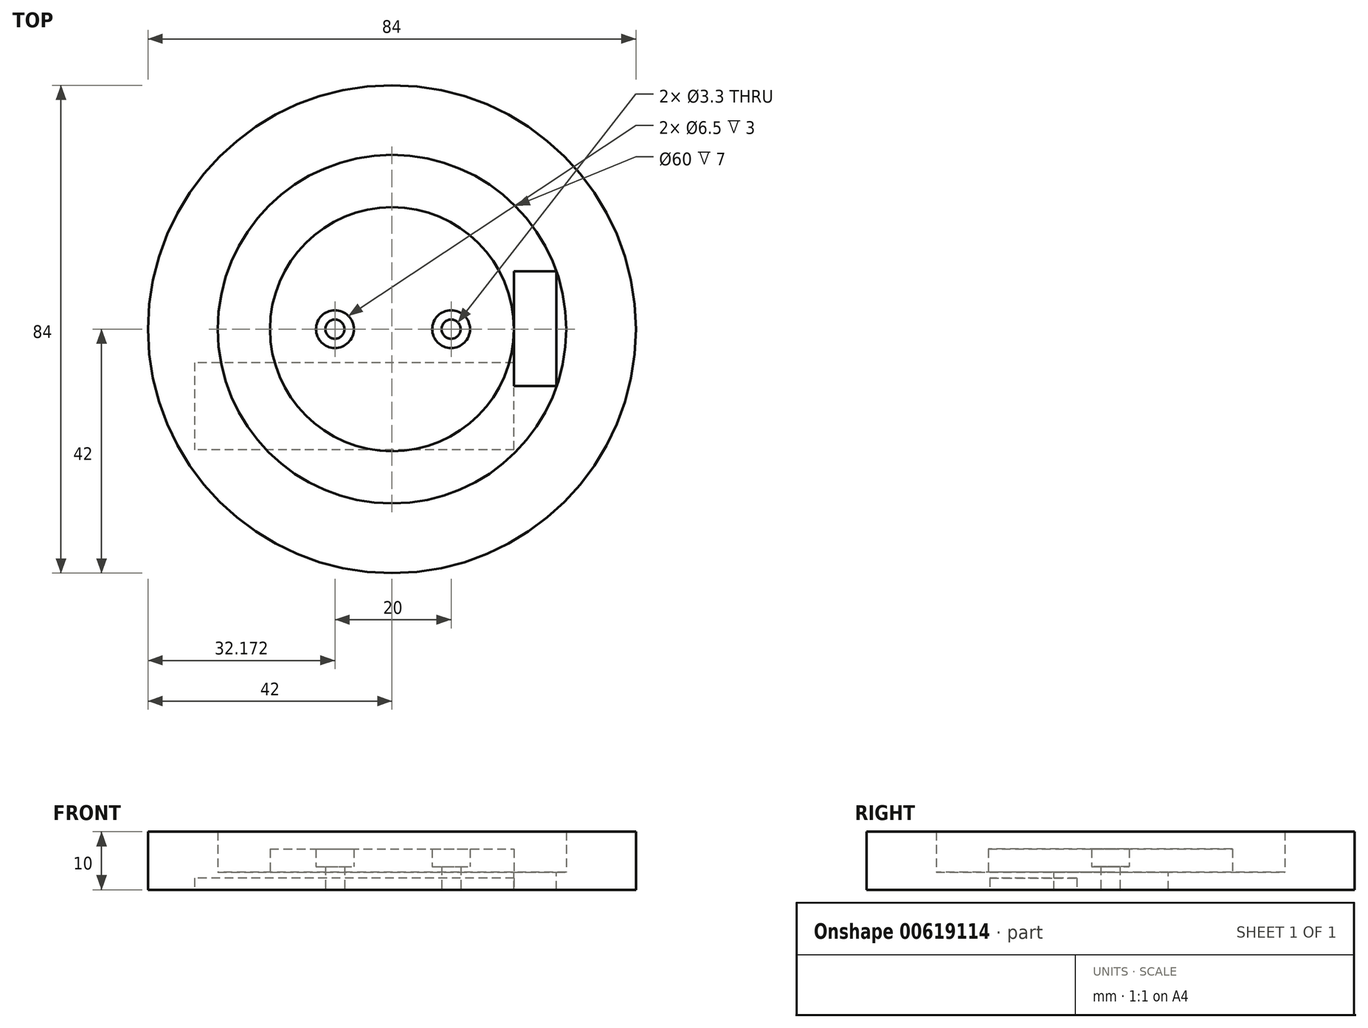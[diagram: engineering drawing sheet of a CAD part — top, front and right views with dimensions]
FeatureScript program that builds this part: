
annotation { "Feature Type Name" : "Feature", "Feature Type Description" : "" }
export const myFeature = defineFeature(function(context is Context, id is Id, definition is map)
    precondition{}
    {
        {
            var Q0;
            Q0=qCreatedBy(makeId("Front.planeOp"),FACE);
            var sketch = newSketch(context, id + "F0", { "sketchPlane" : qUnion([Q0])});
            skLineSegment(sketch, "E0", {"start": v(0, 0) * mm, "end": v(0, 7) * mm});
            skLineSegment(sketch, "E1", {"start": v(0, 7) * mm, "end": v(-21, 7) * mm});
            skLineSegment(sketch, "E2", {"start": v(-21, 7) * mm, "end": v(-21, 3) * mm});
            skLineSegment(sketch, "E3", {"start": v(-21, 3) * mm, "end": v(-30, 3) * mm});
            skLineSegment(sketch, "E4", {"start": v(-30, 3) * mm, "end": v(-30, 10) * mm});
            skLineSegment(sketch, "E5", {"start": v(-30, 10) * mm, "end": v(-42, 10) * mm});
            skLineSegment(sketch, "E6", {"start": v(-42, 10) * mm, "end": v(-42, 0) * mm});
            skLineSegment(sketch, "E7", {"start": v(-42, 0) * mm, "end": v(0, 0) * mm});
            skSolve(sketch);
        }
        {
            var Q0;
            Q0 = qSketchRegion(id + "F0", true);
            var Q1;
            Q1=sQuery(id+"F0.wireOp",EDGE,"E0");
            revolve(context, id + "F1", {"entities" : qUnion([Q0]), "axis" : qUnion([Q1]), "revolveType" : RevolveType.FULL});
        }
        {
            var Q0;
            Q0=makeQuery(id+"F1.opRevolve","SWEPT_FACE",FACE,{"disambiguationData":[OSD([sQuery(id+"F0.wireOp",EDGE,"E3")])]});
            var sketch = newSketch(context, id + "F2", { "sketchPlane" : qUnion([Q0])});
            skLineSegment(sketch, "E8.bottom", {"start": v(21, 0) * mm, "end": v(28.3, 0) * mm});
            skLineSegment(sketch, "E8.top", {"start": v(21, 9.97) * mm, "end": v(28.3, 9.97) * mm});
            skLineSegment(sketch, "E8.left", {"start": v(21, 0) * mm, "end": v(21, 9.97) * mm});
            skLineSegment(sketch, "E8.right", {"start": v(28.3, 0) * mm, "end": v(28.3, 9.97) * mm});
            skLineSegment(sketch, "E9.bottom", {"start": v(28.3, 0) * mm, "end": v(21, 0) * mm});
            skLineSegment(sketch, "E9.top", {"start": v(28.3, -9.76) * mm, "end": v(21, -9.76) * mm});
            skLineSegment(sketch, "E9.left", {"start": v(28.3, 0) * mm, "end": v(28.3, -9.76) * mm});
            skLineSegment(sketch, "E9.right", {"start": v(21, 0) * mm, "end": v(21, -9.76) * mm});
            skSolve(sketch);
        }
        {
            var Q0;
            Q0 = qSketchRegion(id + "F2", true);
            extrude(context, id + "F3", {"entities" : qUnion([Q0]), "operationType" : NewBodyOperationType.REMOVE, "oppositeDirection" : true, "depth" : 25 * mm, "offsetDistance" : 25 * mm});
        }
        {
            var Q0;
            Q0=makeQuery(id+"F1.opRevolve","SWEPT_FACE",FACE,{"disambiguationData":[OSD([sQuery(id+"F0.wireOp",EDGE,"E7")])]});
            var sketch = newSketch(context, id + "F4", { "sketchPlane" : qUnion([Q0])});
            skLineSegment(sketch, "E10.bottom", {"start": v(21, 5.77) * mm, "end": v(-34, 5.77) * mm});
            skLineSegment(sketch, "E10.top", {"start": v(21, 20.77) * mm, "end": v(-34, 20.77) * mm});
            skLineSegment(sketch, "E10.left", {"start": v(21, 5.77) * mm, "end": v(21, 20.77) * mm});
            skLineSegment(sketch, "E10.right", {"start": v(-34, 5.77) * mm, "end": v(-34, 20.77) * mm});
            skSolve(sketch);
        }
        {
            var Q0;
            Q0 = qSketchRegion(id + "F4", true);
            extrude(context, id + "F5", {"entities" : qUnion([Q0]), "operationType" : NewBodyOperationType.REMOVE, "oppositeDirection" : true, "depth" : 2 * mm, "offsetDistance" : 25 * mm});
        }
        {
            var Q0;
            Q0=makeQuery(id+"F1.opRevolve","SWEPT_FACE",FACE,{"disambiguationData":[OSD([sQuery(id+"F0.wireOp",EDGE,"E1")])]});
            var sketch = newSketch(context, id + "F6", { "sketchPlane" : qUnion([Q0])});
            skPoint(sketch, "E11", {"position": v(-9.83, 0) * mm});
            skPoint(sketch, "E12", {"position": v(10.17, 0) * mm});
            skSolve(sketch);
        }
        {
            var Q0;
            Q0=sQuery(id+"F6.wireOp",VERTEX,"E11");
            var Q1;
            Q1=sQuery(id+"F6.wireOp",VERTEX,"E12");
            var Q2;
            Q2=makeQuery(id+"F1.opRevolve","SWEPT_BODY",BODY,{"disambiguationData":[OSD([sQuery(id+"F0.wireOp",EDGE,"E0"),sQuery(id+"F0.wireOp",EDGE,"E1"),sQuery(id+"F0.wireOp",EDGE,"E2"),sQuery(id+"F0.wireOp",EDGE,"E3"),sQuery(id+"F0.wireOp",EDGE,"E4"),sQuery(id+"F0.wireOp",EDGE,"E5"),sQuery(id+"F0.wireOp",EDGE,"E6"),sQuery(id+"F0.wireOp",EDGE,"E7")])]});
            hole(context, id + "F7", {"style" : HoleStyle.C_BORE, "endStyle" : HoleEndStyle.THROUGH, "standardTappedOrClearance" : lookupTablePath({ "standard" : "ISO", "fit" : "Normal", "size" : "M3", "type" : "Clearance" }), "standardBlindInLast" : lookupTablePath({ "fit" : "Standard", "standard" : "ISO", "size" : "M3", "type" : "Clearance" }), "holeDiameter" : 3.3 * mm, "cBoreDiameter" : 6.5 * mm, "cBoreDepth" : 3 * mm, "majorDiameter" : 3 * mm, "isTappedThrough" : true, "tappedDepth" : 12 * mm, "tapClearance" : 3, "locations" : qUnion([Q0, Q1]), "scope" : qUnion([Q2]), "startStyle" : HoleStartStyle.SKETCH});
        }
    });
